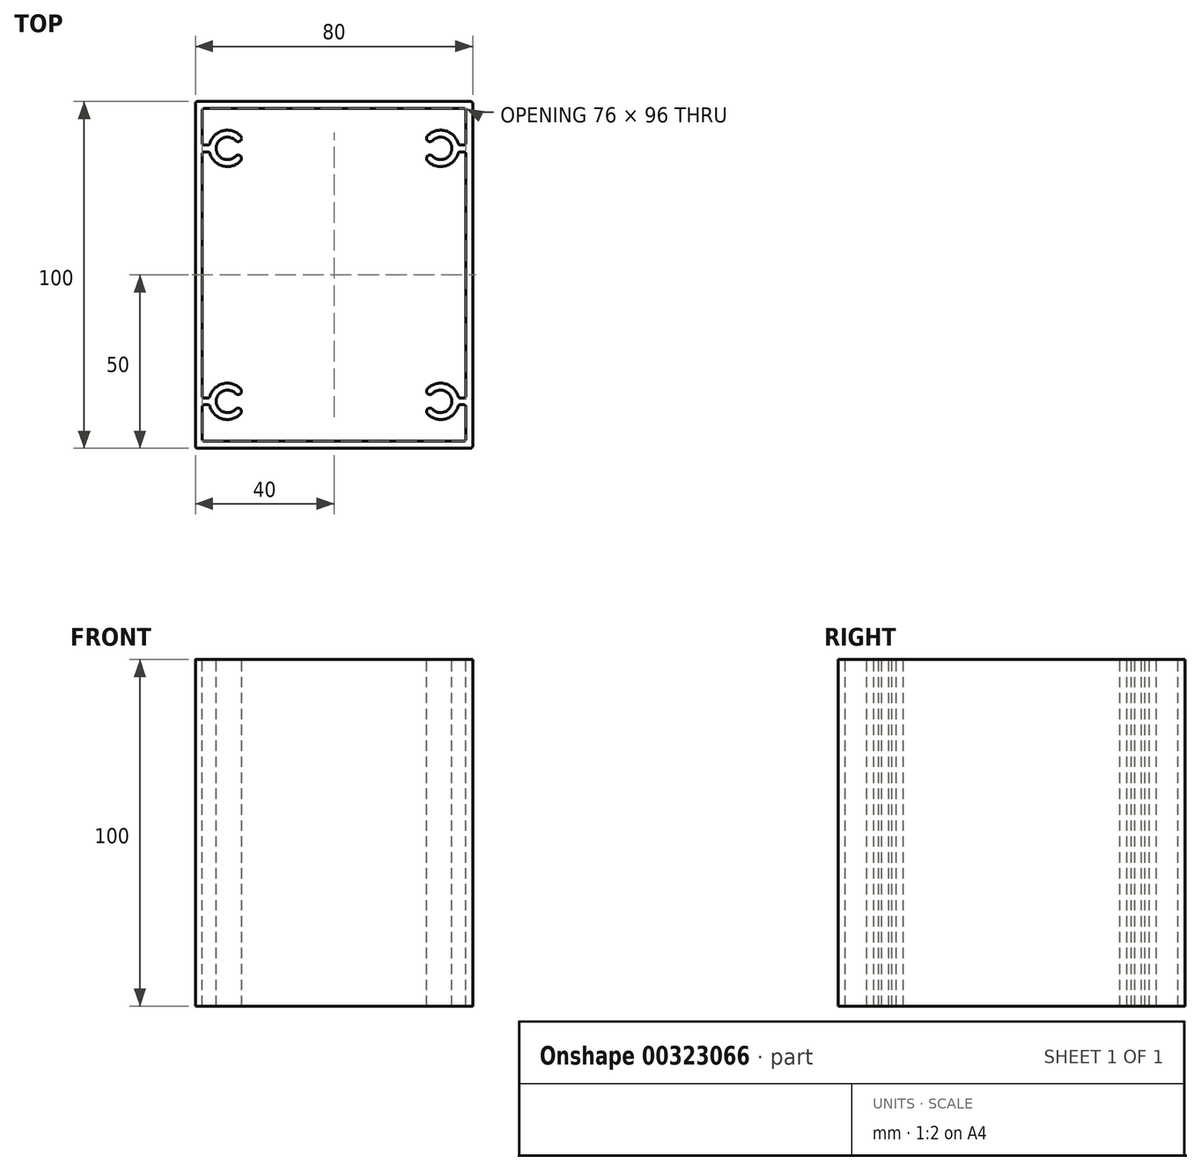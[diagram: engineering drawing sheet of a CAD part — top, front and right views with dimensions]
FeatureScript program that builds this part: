
annotation { "Feature Type Name" : "Feature", "Feature Type Description" : "" }
export const myFeature = defineFeature(function(context is Context, id is Id, definition is map)
    precondition{}
    {
        {
            var Q0;
            Q0=qCreatedBy(makeId("Top.planeOp"),FACE);
            var sketch = newSketch(context, id + "F0", { "sketchPlane" : qUnion([Q0])});
            skLineSegment(sketch, "E0", {"start": v(40, 49.5) * mm, "end": v(40, -49.5) * mm});
            skLineSegment(sketch, "E1", {"start": v(39.5, -50) * mm, "end": v(-39.5, -50) * mm});
            skLineSegment(sketch, "E2", {"start": v(-40, -49.5) * mm, "end": v(-40, 49.5) * mm});
            skLineSegment(sketch, "E3", {"start": v(-39.5, 50) * mm, "end": v(39.5, 50) * mm});
            skLineSegment(sketch, "E4", {"start": v(38, 47.5) * mm, "end": v(38, 38) * mm});
            skLineSegment(sketch, "E5", {"start": v(-37.5, 48) * mm, "end": v(37.5, 48) * mm});
            skLineSegment(sketch, "E6", {"start": v(37.5, -48) * mm, "end": v(-37.5, -48) * mm});
            skLineSegment(sketch, "E7", {"start": v(-38, -47.5) * mm, "end": v(-38, -38) * mm});
            skArc(sketch, "E8", {"start": v(28.4, -38.74) * mm, "mid": v(34, -36.5) * mm, "end": v(28.4, -34.26) * mm});
            skArc(sketch, "E9", {"start": v(28.4, -38.74) * mm, "mid": v(27.82, -38.44) * mm, "end": v(27.17, -38.57) * mm});
            skArc(sketch, "E10", {"start": v(27.17, -34.43) * mm, "mid": v(27.82, -34.56) * mm, "end": v(28.4, -34.26) * mm});
            skArc(sketch, "E11", {"start": v(26.95, -40.12) * mm, "mid": v(32.04, -41.59) * mm, "end": v(35.82, -37.87) * mm});
            skArc(sketch, "E12", {"start": v(27.17, -38.57) * mm, "mid": v(26.68, -39.29) * mm, "end": v(26.95, -40.12) * mm});
            skArc(sketch, "E13", {"start": v(26.95, -32.88) * mm, "mid": v(26.68, -33.71) * mm, "end": v(27.17, -34.43) * mm});
            skLineSegment(sketch, "E14", {"start": v(27.17, -34.43) * mm, "end": v(30.75, -36.5) * mm, "construction": true});
            skLineSegment(sketch, "E15", {"start": v(30.75, -36.5) * mm, "end": v(27.17, -38.57) * mm, "construction": true});
            skArc(sketch, "E16", {"start": v(28.4, 34.26) * mm, "mid": v(34, 36.5) * mm, "end": v(28.4, 38.74) * mm});
            skArc(sketch, "E17", {"start": v(28.4, 34.26) * mm, "mid": v(27.82, 34.56) * mm, "end": v(27.17, 34.43) * mm});
            skArc(sketch, "E18", {"start": v(27.17, 38.57) * mm, "mid": v(27.82, 38.44) * mm, "end": v(28.4, 38.74) * mm});
            skArc(sketch, "E19", {"start": v(26.95, 32.88) * mm, "mid": v(32.04, 31.41) * mm, "end": v(35.82, 35.13) * mm});
            skArc(sketch, "E20", {"start": v(27.17, 34.43) * mm, "mid": v(26.68, 33.71) * mm, "end": v(26.95, 32.88) * mm});
            skArc(sketch, "E21", {"start": v(26.95, 40.12) * mm, "mid": v(26.68, 39.29) * mm, "end": v(27.17, 38.57) * mm});
            skLineSegment(sketch, "E22", {"start": v(27.17, 38.57) * mm, "end": v(30.75, 36.5) * mm, "construction": true});
            skLineSegment(sketch, "E23", {"start": v(30.75, 36.5) * mm, "end": v(27.17, 34.43) * mm, "construction": true});
            skArc(sketch, "E24", {"start": v(-28.4, 38.74) * mm, "mid": v(-34, 36.5) * mm, "end": v(-28.4, 34.26) * mm});
            skArc(sketch, "E25", {"start": v(-27.17, 34.43) * mm, "mid": v(-27.82, 34.56) * mm, "end": v(-28.4, 34.26) * mm});
            skArc(sketch, "E26", {"start": v(-28.4, 38.74) * mm, "mid": v(-27.82, 38.44) * mm, "end": v(-27.17, 38.57) * mm});
            skArc(sketch, "E27", {"start": v(-26.95, 40.12) * mm, "mid": v(-32.04, 41.59) * mm, "end": v(-35.82, 37.87) * mm});
            skArc(sketch, "E28", {"start": v(-26.95, 32.88) * mm, "mid": v(-26.68, 33.71) * mm, "end": v(-27.17, 34.43) * mm});
            skArc(sketch, "E29", {"start": v(-27.17, 38.57) * mm, "mid": v(-26.68, 39.29) * mm, "end": v(-26.95, 40.12) * mm});
            skLineSegment(sketch, "E30", {"start": v(-27.17, 38.57) * mm, "end": v(-30.75, 36.5) * mm, "construction": true});
            skLineSegment(sketch, "E31", {"start": v(-30.75, 36.5) * mm, "end": v(-27.17, 34.43) * mm, "construction": true});
            skArc(sketch, "E32", {"start": v(-28.4, -34.26) * mm, "mid": v(-34, -36.5) * mm, "end": v(-28.4, -38.74) * mm});
            skArc(sketch, "E33", {"start": v(-27.17, -38.57) * mm, "mid": v(-27.82, -38.44) * mm, "end": v(-28.4, -38.74) * mm});
            skArc(sketch, "E34", {"start": v(-28.4, -34.26) * mm, "mid": v(-27.82, -34.56) * mm, "end": v(-27.17, -34.43) * mm});
            skArc(sketch, "E35", {"start": v(-26.95, -32.88) * mm, "mid": v(-32.04, -31.41) * mm, "end": v(-35.82, -35.13) * mm});
            skArc(sketch, "E36", {"start": v(-26.95, -40.12) * mm, "mid": v(-26.68, -39.29) * mm, "end": v(-27.17, -38.57) * mm});
            skArc(sketch, "E37", {"start": v(-27.17, -34.43) * mm, "mid": v(-26.68, -33.71) * mm, "end": v(-26.95, -32.88) * mm});
            skLineSegment(sketch, "E38", {"start": v(-27.17, -34.43) * mm, "end": v(-30.75, -36.5) * mm, "construction": true});
            skLineSegment(sketch, "E39", {"start": v(-30.75, -36.5) * mm, "end": v(-27.17, -38.57) * mm, "construction": true});
            skLineSegment(sketch, "E40", {"start": v(37.5, 35.5) * mm, "end": v(36.3, 35.5) * mm});
            skLineSegment(sketch, "E41", {"start": v(37.5, 37.5) * mm, "end": v(36.3, 37.5) * mm});
            skLineSegment(sketch, "E42", {"start": v(37.5, -35.5) * mm, "end": v(36.3, -35.5) * mm});
            skLineSegment(sketch, "E43", {"start": v(37.5, -37.5) * mm, "end": v(36.3, -37.5) * mm});
            skLineSegment(sketch, "E44", {"start": v(38, 35) * mm, "end": v(38, -35) * mm});
            skLineSegment(sketch, "E45", {"start": v(-38, 38) * mm, "end": v(-38, 47.5) * mm});
            skLineSegment(sketch, "E46", {"start": v(-36.3, 37.5) * mm, "end": v(-37.5, 37.5) * mm});
            skLineSegment(sketch, "E47", {"start": v(-36.3, 35.5) * mm, "end": v(-37.5, 35.5) * mm});
            skArc(sketch, "E48", {"start": v(35.82, 37.87) * mm, "mid": v(32.04, 41.59) * mm, "end": v(26.95, 40.12) * mm});
            skArc(sketch, "E49", {"start": v(-35.82, 35.13) * mm, "mid": v(-32.04, 31.41) * mm, "end": v(-26.95, 32.88) * mm});
            skLineSegment(sketch, "E50", {"start": v(38, -38) * mm, "end": v(38, -47.5) * mm});
            skArc(sketch, "E51", {"start": v(35.82, -35.13) * mm, "mid": v(32.04, -31.41) * mm, "end": v(26.95, -32.88) * mm});
            skLineSegment(sketch, "E52", {"start": v(-38, -35) * mm, "end": v(-38, 35) * mm});
            skArc(sketch, "E53", {"start": v(-35.82, -37.87) * mm, "mid": v(-32.04, -41.59) * mm, "end": v(-26.95, -40.12) * mm});
            skLineSegment(sketch, "E54", {"start": v(-36.3, -35.5) * mm, "end": v(-37.5, -35.5) * mm});
            skLineSegment(sketch, "E55", {"start": v(-36.3, -37.5) * mm, "end": v(-37.5, -37.5) * mm});
            skArc(sketch, "E56", {"start": v(40, 49.5) * mm, "mid": v(39.85, 49.85) * mm, "end": v(39.5, 50) * mm});
            skArc(sketch, "E57", {"start": v(39.5, -50) * mm, "mid": v(39.85, -49.85) * mm, "end": v(40, -49.5) * mm});
            skArc(sketch, "E58", {"start": v(-39.5, 50) * mm, "mid": v(-39.85, 49.85) * mm, "end": v(-40, 49.5) * mm});
            skArc(sketch, "E59", {"start": v(-40, -49.5) * mm, "mid": v(-39.85, -49.85) * mm, "end": v(-39.5, -50) * mm});
            skLineSegment(sketch, "E60", {"start": v(0, 53) * mm, "end": v(0, -53) * mm, "construction": true});
            skLineSegment(sketch, "E61", {"start": v(34.3, 36.5) * mm, "end": v(-34.3, 36.5) * mm, "construction": true});
            skLineSegment(sketch, "E62", {"start": v(34.3, -36.5) * mm, "end": v(-34.3, -36.5) * mm, "construction": true});
            skLineSegment(sketch, "E63", {"start": v(30.75, 40.05) * mm, "end": v(30.75, 32.95) * mm, "construction": true});
            skLineSegment(sketch, "E64", {"start": v(-30.75, 40.05) * mm, "end": v(-30.75, 32.95) * mm, "construction": true});
            skLineSegment(sketch, "E65", {"start": v(-30.75, -32.95) * mm, "end": v(-30.75, -40.05) * mm, "construction": true});
            skLineSegment(sketch, "E66", {"start": v(30.75, -32.95) * mm, "end": v(30.75, -40.05) * mm, "construction": true});
            skLineSegment(sketch, "E67", {"start": v(43, 0) * mm, "end": v(-43, 0) * mm, "construction": true});
            skArc(sketch, "E68", {"start": v(38, 47.5) * mm, "mid": v(37.85, 47.85) * mm, "end": v(37.5, 48) * mm});
            skArc(sketch, "E69", {"start": v(37.5, 37.5) * mm, "mid": v(37.85, 37.65) * mm, "end": v(38, 38) * mm});
            skArc(sketch, "E70", {"start": v(35.82, 37.87) * mm, "mid": v(36, 37.6) * mm, "end": v(36.3, 37.5) * mm});
            skArc(sketch, "E71", {"start": v(36.3, 35.5) * mm, "mid": v(36, 35.4) * mm, "end": v(35.82, 35.13) * mm});
            skArc(sketch, "E72", {"start": v(38, 35) * mm, "mid": v(37.85, 35.35) * mm, "end": v(37.5, 35.5) * mm});
            skArc(sketch, "E73", {"start": v(37.5, -35.5) * mm, "mid": v(37.85, -35.35) * mm, "end": v(38, -35) * mm});
            skArc(sketch, "E74", {"start": v(35.82, -35.13) * mm, "mid": v(36, -35.4) * mm, "end": v(36.3, -35.5) * mm});
            skArc(sketch, "E75", {"start": v(38, -38) * mm, "mid": v(37.85, -37.65) * mm, "end": v(37.5, -37.5) * mm});
            skArc(sketch, "E76", {"start": v(36.3, -37.5) * mm, "mid": v(36, -37.6) * mm, "end": v(35.82, -37.87) * mm});
            skArc(sketch, "E77", {"start": v(37.5, -48) * mm, "mid": v(37.85, -47.85) * mm, "end": v(38, -47.5) * mm});
            skArc(sketch, "E78", {"start": v(-36.3, 37.5) * mm, "mid": v(-36, 37.6) * mm, "end": v(-35.82, 37.87) * mm});
            skArc(sketch, "E79", {"start": v(-38, 38) * mm, "mid": v(-37.85, 37.65) * mm, "end": v(-37.5, 37.5) * mm});
            skArc(sketch, "E80", {"start": v(-37.5, 48) * mm, "mid": v(-37.85, 47.85) * mm, "end": v(-38, 47.5) * mm});
            skArc(sketch, "E81", {"start": v(-35.82, 35.13) * mm, "mid": v(-36, 35.4) * mm, "end": v(-36.3, 35.5) * mm});
            skArc(sketch, "E82", {"start": v(-37.5, 35.5) * mm, "mid": v(-37.85, 35.35) * mm, "end": v(-38, 35) * mm});
            skArc(sketch, "E83", {"start": v(-36.3, -35.5) * mm, "mid": v(-36, -35.4) * mm, "end": v(-35.82, -35.13) * mm});
            skArc(sketch, "E84", {"start": v(-38, -35) * mm, "mid": v(-37.85, -35.35) * mm, "end": v(-37.5, -35.5) * mm});
            skArc(sketch, "E85", {"start": v(-35.82, -37.87) * mm, "mid": v(-36, -37.6) * mm, "end": v(-36.3, -37.5) * mm});
            skArc(sketch, "E86", {"start": v(-37.5, -37.5) * mm, "mid": v(-37.85, -37.65) * mm, "end": v(-38, -38) * mm});
            skArc(sketch, "E87", {"start": v(-38, -47.5) * mm, "mid": v(-37.85, -47.85) * mm, "end": v(-37.5, -48) * mm});
            skSolve(sketch);
        }
        {
            var Q0;
            Q0=makeQuery(id+"F0.imprint","IMPRINT",FACE,{"disambiguationData":[TD([[makeQuery(id+"F0.imprint","IMPRINT",EDGE,{"derivedFrom":sQuery(id+"F0.wireOp",EDGE,"E0")}),-1.0]])]});
            extrude(context, id + "F1", {"entities" : qUnion([Q0]), "oppositeDirection" : true, "depth" : 100 * mm});
        }
    });
